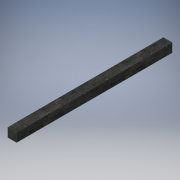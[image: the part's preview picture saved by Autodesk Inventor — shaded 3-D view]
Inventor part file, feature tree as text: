
AUTODESK INVENTOR PART (.ipt)
format: ipt  version: 2019 (Build 230136000, 136)  size: 100,352 bytes
history: native  units: mm
features: extrude x1, sketch x1
ambient origin geometry x8: Origin, YZ Plane, XZ Plane, XY Plane, X Axis, Y Axis, Z Axis, Center Point
bodies: Solid1 (feature_tree)
feature tree (2):
  extrude  "Extrusion1"  Depth=335.0mm
  sketch  "Sketch1"  dims[d0=19.0mm d1=335.0mm d2=19.0mm d3=0.0mm]
